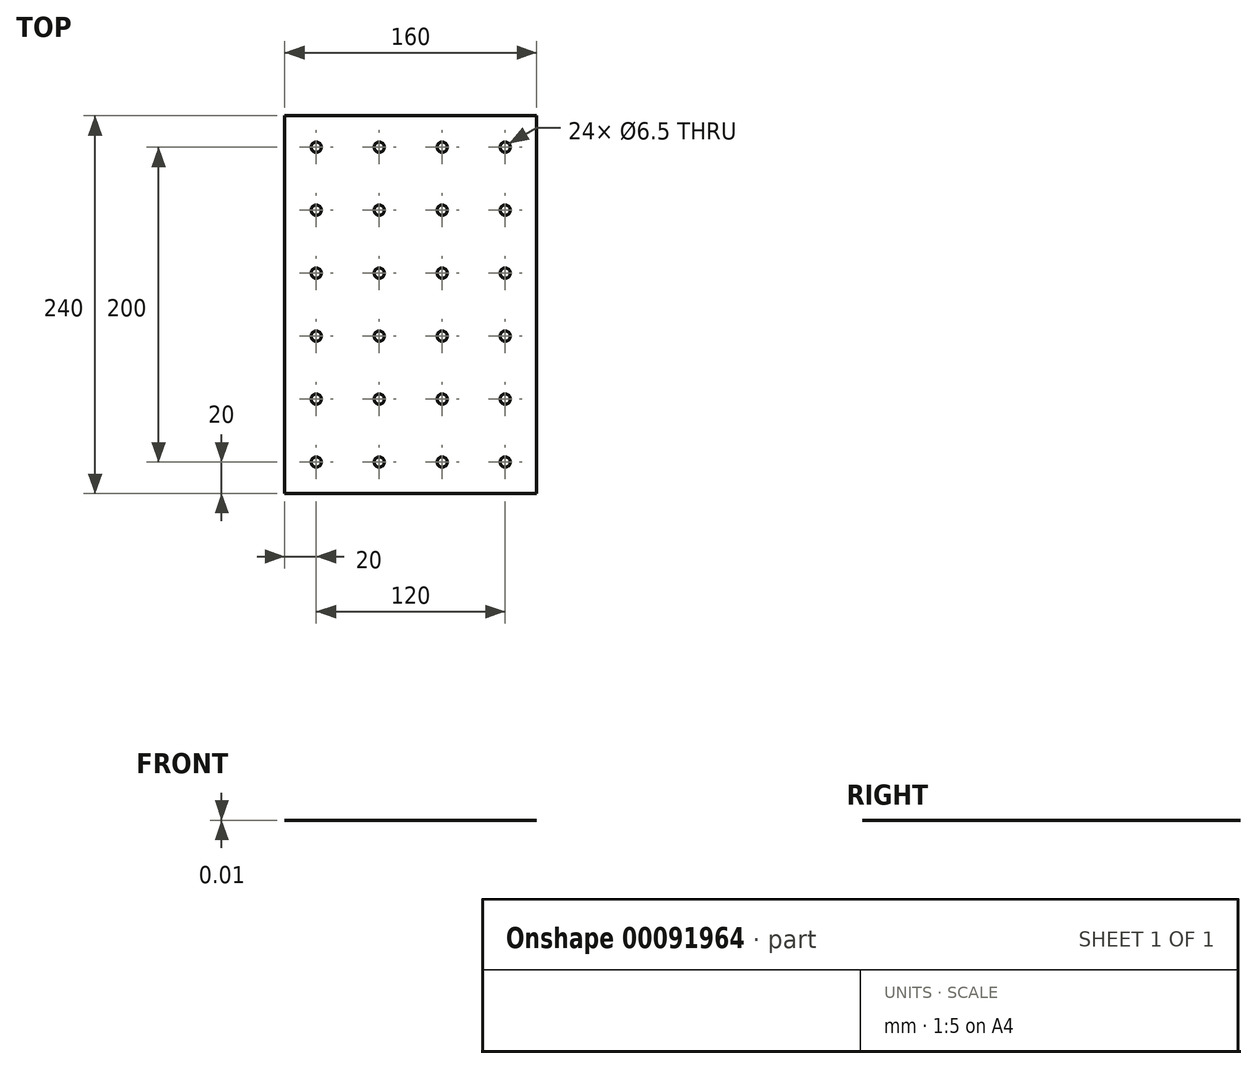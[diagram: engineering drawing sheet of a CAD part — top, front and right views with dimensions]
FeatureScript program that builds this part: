
annotation { "Feature Type Name" : "Feature", "Feature Type Description" : "" }
export const myFeature = defineFeature(function(context is Context, id is Id, definition is map)
    precondition{}
    {
        {
            var Q0;
            Q0=qCreatedBy(makeId("Top.planeOp"),FACE);
            var sketch = newSketch(context, id + "F0", { "sketchPlane" : qUnion([Q0])});
            skLineSegment(sketch, "E0.bottom", {"start": v(80, 120) * mm, "end": v(-80, 120) * mm});
            skLineSegment(sketch, "E0.top", {"start": v(80, -120) * mm, "end": v(-80, -120) * mm});
            skLineSegment(sketch, "E0.left", {"start": v(80, 120) * mm, "end": v(80, -120) * mm});
            skLineSegment(sketch, "E0.right", {"start": v(-80, 120) * mm, "end": v(-80, -120) * mm});
            skPoint(sketch, "E0.middle", {"position": v(0, 0) * mm});
            skLineSegment(sketch, "E1.bottom", {"start": v(0, 0) * mm, "end": v(-60, 0) * mm, "construction": true});
            skLineSegment(sketch, "E1.top", {"start": v(0, -100) * mm, "end": v(-60, -100) * mm, "construction": true});
            skLineSegment(sketch, "E1.left", {"start": v(0, 0) * mm, "end": v(0, -100) * mm, "construction": true});
            skLineSegment(sketch, "E1.right", {"start": v(-60, 0) * mm, "end": v(-60, -100) * mm, "construction": true});
            skCircle(sketch, "E2", {"center": v(-60, -100) * mm, "radius": 3.25 * mm});
            skCircle(sketch, "E3.0.1.0", {"center": v(-60, -60) * mm, "radius": 3.25 * mm});
            skCircle(sketch, "E3.0.2.0", {"center": v(-60, -20) * mm, "radius": 3.25 * mm});
            skCircle(sketch, "E3.0.3.0", {"center": v(-60, 20) * mm, "radius": 3.25 * mm});
            skCircle(sketch, "E3.0.4.0", {"center": v(-60, 60) * mm, "radius": 3.25 * mm});
            skCircle(sketch, "E3.0.5.0", {"center": v(-60, 100) * mm, "radius": 3.25 * mm});
            skCircle(sketch, "E3.1.0.0", {"center": v(-20, -100) * mm, "radius": 3.25 * mm});
            skCircle(sketch, "E3.1.1.0", {"center": v(-20, -60) * mm, "radius": 3.25 * mm});
            skCircle(sketch, "E3.1.2.0", {"center": v(-20, -20) * mm, "radius": 3.25 * mm});
            skCircle(sketch, "E3.1.3.0", {"center": v(-20, 20) * mm, "radius": 3.25 * mm});
            skCircle(sketch, "E3.1.4.0", {"center": v(-20, 60) * mm, "radius": 3.25 * mm});
            skCircle(sketch, "E3.1.5.0", {"center": v(-20, 100) * mm, "radius": 3.25 * mm});
            skCircle(sketch, "E3.2.0.0", {"center": v(20, -100) * mm, "radius": 3.25 * mm});
            skCircle(sketch, "E3.2.1.0", {"center": v(20, -60) * mm, "radius": 3.25 * mm});
            skCircle(sketch, "E3.2.2.0", {"center": v(20, -20) * mm, "radius": 3.25 * mm});
            skCircle(sketch, "E3.2.3.0", {"center": v(20, 20) * mm, "radius": 3.25 * mm});
            skCircle(sketch, "E3.2.4.0", {"center": v(20, 60) * mm, "radius": 3.25 * mm});
            skCircle(sketch, "E3.2.5.0", {"center": v(20, 100) * mm, "radius": 3.25 * mm});
            skCircle(sketch, "E3.3.0.0", {"center": v(60, -100) * mm, "radius": 3.25 * mm});
            skCircle(sketch, "E3.3.1.0", {"center": v(60, -60) * mm, "radius": 3.25 * mm});
            skCircle(sketch, "E3.3.2.0", {"center": v(60, -20) * mm, "radius": 3.25 * mm});
            skCircle(sketch, "E3.3.3.0", {"center": v(60, 20) * mm, "radius": 3.25 * mm});
            skCircle(sketch, "E3.3.4.0", {"center": v(60, 60) * mm, "radius": 3.25 * mm});
            skCircle(sketch, "E3.3.5.0", {"center": v(60, 100) * mm, "radius": 3.25 * mm});
            skLineSegment(sketch, "E3.direction1", {"start": v(-60, -100) * mm, "end": v(-20, -100) * mm, "construction": true});
            skLineSegment(sketch, "E3.direction2", {"start": v(-60, -100) * mm, "end": v(-60, -60) * mm, "construction": true});
            skSolve(sketch);
        }
        {
            var Q0;
            Q0=makeQuery(id+"F0.imprint","IMPRINT",FACE,{"disambiguationData":[TD([[makeQuery(id+"F0.imprint","IMPRINT",EDGE,{"derivedFrom":sQuery(id+"F0.wireOp",EDGE,"E0.bottom")}),1.0]])]});
            extrude(context, id + "F1", {"entities" : qUnion([Q0]), "depth" : 1 / 101.6 * mm});
        }
    });
